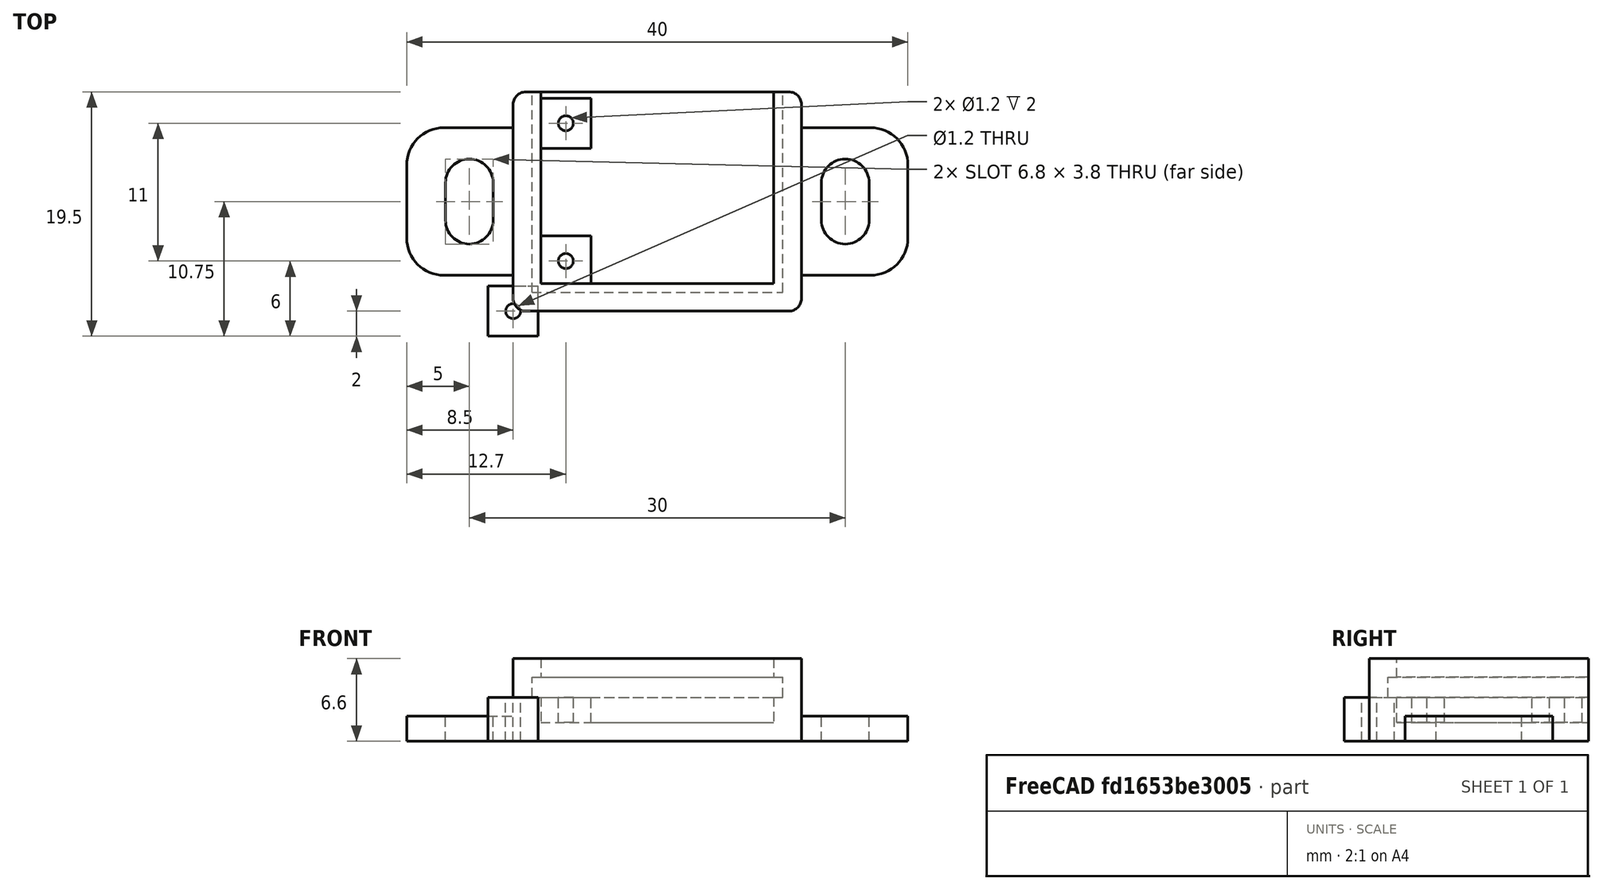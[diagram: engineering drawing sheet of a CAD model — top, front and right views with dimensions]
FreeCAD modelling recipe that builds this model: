
FCSTD DOCUMENT  (FreeCAD 0.19R)
Label: buzzer
License: FreeArt
LicenseURL: http://artlibre.org/licence/lal
objects: Part::Box×4, Part::MultiFuse×3, Part::Cut×2, Spreadsheet::Sheet×1, Part::Fillet×1, Part::Cylinder×1, Part::FeaturePython×1, Part::Feature×1, App::Part×1
note: 12 computed .brp shape members not serialized (recipe doc carries the construction recipe); baked Part::Feature solids carry a one-line shape summary decoded from their .brp

FEATURE [Spreadsheet::Sheet] Spreadsheet  label="p"
  cells = A1=pcb_x; B1(pcb_x)=20; A2=pcb_y; B2(pcb_y)=16; A3=pcb_z; B3(pcb_z)=1.6; A4=pcb_under; B4(pcb_under)=2; A5=side_wall; B5(side_wall)=1.5; A6=pcb_side_lane; B6(pcb_side_lane)=0.7; A7=bottom_wall; B7(bottom_wall)=1.5; A8=pcb_above; B8(pcb_above)=1.5; A9=hole_dist_y; B9(hole_dist_y)=11; A10=hole_r; B10(hole_r)=0.6; A11=hole_off_x; B11(hole_off_x)=2; A12=hole_stand_size; B12(hole_stand_size)=4
FEATURE [Part::Box] Box  label="external cube"
  AttacherType = Attacher::AttachEngine3D
  Height = 6.6
  Length = 23
  Width = 17.5
  expr: Height = <<p>>.bottom_wall + <<p>>.pcb_under + <<p>>.pcb_z + <<p>>.pcb_above
  expr: Width = <<p>>.pcb_y + <<p>>.side_wall
  expr: Length = <<p>>.pcb_x + 2 * <<p>>.side_wall
FEATURE [Part::Box] Box006  label="internal cube"
  AttacherType = Attacher::AttachEngine3D
  Height = 5.1
  Length = 18.6
  Placement = pos=(2.2,2.2,1.5) rot=(0,0,1;0rad)
  Width = 16.1
  expr: .Placement.Base.y = <<p>>.side_wall + <<p>>.pcb_side_lane
  expr: .Placement.Base.x = <<p>>.side_wall + <<p>>.pcb_side_lane
  expr: .Placement.Base.z = <<p>>.bottom_wall
  expr: Height = <<p>>.pcb_under + <<p>>.pcb_z + <<p>>.pcb_above
  expr: Width = <<p>>.pcb_y - 2 * <<p>>.pcb_side_lane + <<p>>.side_wall
  expr: Length = <<p>>.pcb_x - 2 * <<p>>.pcb_side_lane
FEATURE [Part::Box] Box007  label="pcb extract cube"
  AttacherType = Attacher::AttachEngine3D
  Height = 1.6
  Length = 20
  Placement = pos=(1.5,1.5,3.5) rot=(0,0,1;0rad)
  Width = 16
  expr: .Placement.Base.y = <<p>>.side_wall
  expr: .Placement.Base.x = <<p>>.side_wall
  expr: Length = <<p>>.pcb_x
  expr: Width = <<p>>.pcb_y
  expr: .Placement.Base.z = <<p>>.bottom_wall + <<p>>.pcb_under
  expr: Height = <<p>>.pcb_z
FEATURE [Part::MultiFuse] Fusion  label="extract fusion"
  Shapes = -> [Box006,Box007]
FEATURE [Part::Fillet] Fillet  label="external fillet"
  Base = -> Box
  Edges = 4 edges r=1: [Edge1,Edge3,Edge5,Edge7]
FEATURE [Part::Cylinder] Cylinder  label="hole"
  Angle = 360
  AttacherType = Attacher::AttachEngine3D
  Height = 10
  Radius = 0.6
  expr: Radius = <<p>>.hole_r
FEATURE [Part::Box] Box008  label="stand"
  AttacherType = Attacher::AttachEngine3D
  Height = 3.5
  Length = 4
  Placement = pos=(-2,-2,0) rot=(0,0,1;0rad)
  Width = 4
  expr: Height = <<p>>.pcb_under + <<p>>.bottom_wall
  expr: Length = <<p>>.hole_stand_size
  expr: Width = <<p>>.hole_stand_size
  expr: .Placement.Base.x = -<<p>>.hole_stand_size / 2
  expr: .Placement.Base.y = -<<p>>.hole_stand_size / 2
FEATURE [Part::Cut] Cut003002  label="stand hole cut"
  Base = -> Box008
  Tool = -> Cylinder
FEATURE [Part::FeaturePython] Array  label="hole array"  # Draft array (typed FeaturePython)
  Angle = 360
  ArrayType = 0
  Axis = (0,0,1)
  Base = -> Cut003002
  Center = (0,0,0)
  Count = 2
  ExpandArray = false
  Fuse = false
  IntervalAxis = (0,0,0)
  IntervalX = (1,0,0)
  IntervalY = (0,11,0)
  IntervalZ = (0,0,100)
  NumberCircles = 3
  NumberPolar = 5
  NumberX = 1
  NumberY = 2
  NumberZ = 1
  Placement = pos=(4.2,4,0) rot=(0,0,1;0rad)
  PlacementList = 2 placements: [(0,0,0),(0,11,0)]
  RadialDistance = 50
  ScaleList = (2) [(1,1,1),(1,1,1)]
  Symmetry = 1
  TangentialDistance = 25
  expr: .Placement.Base.y = (2 * <<p>>.side_wall + <<p>>.pcb_y - <<p>>.hole_dist_y) / 2
  expr: .Placement.Base.x = <<p>>.hole_off_x + <<p>>.side_wall + <<p>>.pcb_side_lane
  expr: .IntervalY.y = <<p>>.hole_dist_y
FEATURE [Part::Feature] Cut003003  label="attach plane x dir002"
  Placement = pos=(-8.5,2.85,0) rot=(0,0,1;0rad)
  shape: bbox 40 x 11.8 x 2 mm, 18 faces (baked)
FEATURE [Part::MultiFuse] Fusion001  label="body fusion"
  Shapes = -> [Fillet,Cut003003]
FEATURE [Part::Cut] Cut  label="d4184a cut"
  Base = -> Fusion001
  Tool = -> Fusion
FEATURE [Part::MultiFuse] Fusion002  label="buzzer fusion"
  Shapes = -> [Array,Cut]
FEATURE [App::Part] Part  label="buzzer pcb box part"
  Group = -> [Box,Fillet,Fusion001,Fusion,Box007,Box006,Cut,Cylinder,Box008,Cut003002,Array,Fusion002]
  Origin = -> Origin
